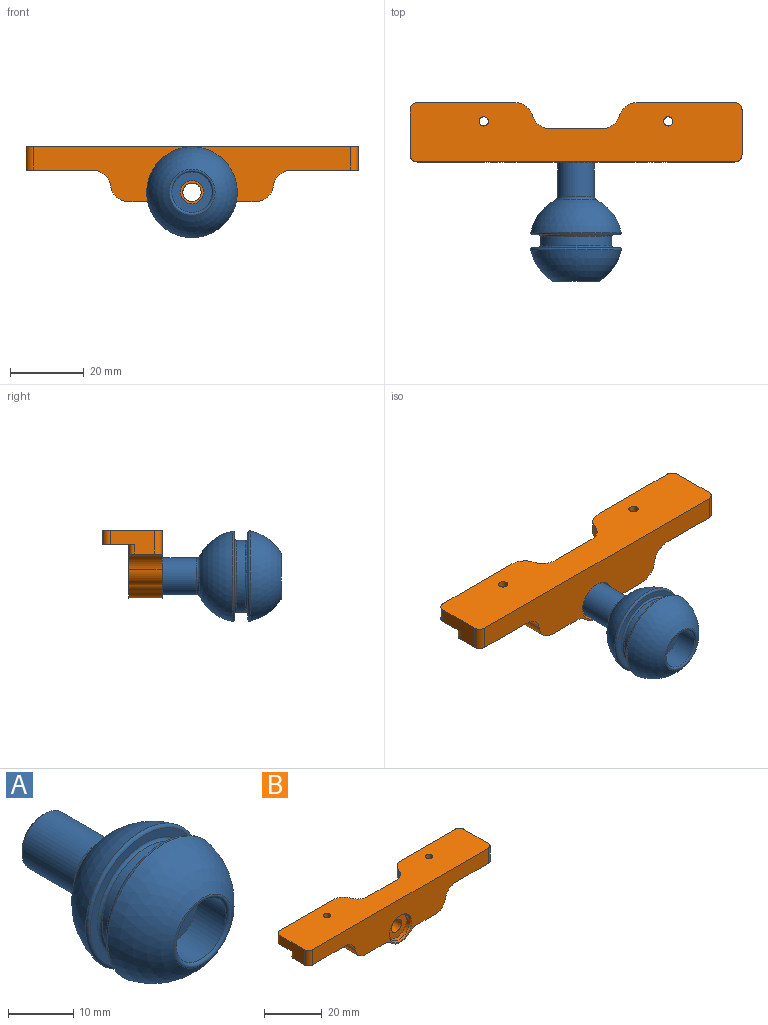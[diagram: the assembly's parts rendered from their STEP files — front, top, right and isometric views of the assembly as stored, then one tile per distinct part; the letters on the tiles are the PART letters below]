
ASSEMBLY  parts=2 mates=1
PART A: 17 faces, bbox 26.6x34.8x26.6 mm
  f0: cylinder r=5mm len=11.36mm, axis (0,-1,0), area 357mm2, adj f15,f16
  f1: sphere r=12.5mm, area 691.3mm2, adj f10,f15
  f2: plane 23.56x23.56mm, normal (0,-1,0), area 105.7mm2, adj f10,f11
  f3: cylinder r=9.75mm len=19.5mm, axis (0,-1,0), area 159.3mm2, adj f11,f12
  f4: plane 23.56x23.56mm, normal (0,1,0), area 105.7mm2, adj f12,f13
  f5: sphere r=12.5mm, area 662.1mm2, adj f13,f14
  f6: cylinder r=5.5mm len=11mm, axis (0,-1,0), area 213.1mm2, adj f7,f14
  f7: plane 11x11mm, normal (0,-1,0), area 63.9mm2, adj f6,f8
  f8: cylinder r=3.15mm len=28.18mm, axis (0,-1,0), area 557.8mm2, adj f7,f9
  f9: plane 9x9mm, normal (0,1,0), area 32.4mm2, adj f8,f16
  f10: torus R=11.78mm, axis (0,-1,0), area 67.1mm2, adj f1,f2
  f11: torus R=10.25mm, axis (0,-1,0), area 49mm2, adj f2,f3
  f12: torus R=10.25mm, axis (0,1,0), area 49mm2, adj f3,f4
  f13: torus R=11.78mm, axis (0,1,0), area 67.1mm2, adj f4,f5
  f14: torus R=6mm, axis (0,1,0), area 38.1mm2, adj f5,f6
  f15: torus R=6mm, axis (0,-1,0), area 36.2mm2, adj f0,f1
  f16: cone r=5mm half-angle=45deg, axis (0,-1,0), area 21.1mm2, adj f0,f9
PART B: 36 faces, bbox 90x16.1x18.4 mm
  f0: cylinder r=2.5mm len=7mm, axis (0,-1,0), area 110mm2, adj f9,f34
  f1: plane 18x9mm, normal (0,0,-1), area 160.7mm2, adj f4,f9,f16,f22,f23,f30
  f2: plane 26.43x3.8mm, normal (0,1,0), area 100.4mm2, adj f5,f11,f14,f25
  f3: plane 12.1x6.4mm, normal (-1,0,0), area 60.3mm2, adj f11,f12,f13,f15,f24,f26
  f4: plane 12.1x6.4mm, normal (1,0,0), area 60.3mm2, adj f1,f11,f14,f16,f23,f25
  f5: cylinder r=5mm len=4.79mm, axis (0,0,-1), area 24.3mm2, adj f2,f6,f11,f14
  f6: cylinder r=5mm len=4.79mm, axis (0,0,-1), area 24.3mm2, adj f5,f9,f11,f14
  f7: cylinder r=5mm len=4.79mm, axis (0,0,-1), area 24.3mm2, adj f8,f9,f11,f13
  f8: cylinder r=5mm len=4.79mm, axis (0,0,-1), area 24.3mm2, adj f7,f10,f11,f13
  f9: plane 87x18.4mm, normal (0,1,0), area 667mm2, adj f0,f1,f6,f7,f11,f12,f13,f14
  f10: plane 26.43x3.8mm, normal (0,1,0), area 100.4mm2, adj f8,f11,f13,f26
  f11: plane 90x16.1mm, normal (0,0,1), area 1268.4mm2, adj f2,f3,f4,f5,f6,f7,f8,f9
  f12: plane 18x9mm, normal (0,0,-1), area 160.7mm2, adj f3,f9,f15,f22,f24,f27
  f13: plane 38x8.6mm, normal (0,0,-1), area 230.5mm2, adj f3,f7,f8,f9,f10,f15,f18,f26
  f14: plane 38x8.6mm, normal (0,0,-1), area 230.5mm2, adj f2,f4,f5,f6,f9,f16,f17,f25
  f15: cylinder r=1.5mm len=2.6mm, axis (0,0,-1), area 6.1mm2, adj f3,f9,f12,f13
  f16: cylinder r=1.5mm len=2.6mm, axis (0,0,1), area 6.1mm2, adj f1,f4,f9,f14
  f17: cylinder r=1.25mm len=3.8mm, axis (0,0,1), area 29.8mm2, adj f11,f14
  f18: cylinder r=1.25mm len=3.8mm, axis (0,0,1), area 29.8mm2, adj f11,f13
  f19: plane 9.15x9mm, normal (0,0,-1), area 82.3mm2, adj f9,f22,f28,f31
  f20: cylinder r=6mm len=9mm, axis (0,1,0), area 87.3mm2, adj f9,f22,f28,f29
  f21: plane 9.15x9mm, normal (0,0,-1), area 82.3mm2, adj f9,f22,f29,f32
  f22: plane 86x18.4mm, normal (0,-1,0), area 862.6mm2, adj f1,f11,f12,f19,f20,f21,f23,f24
  f23: cylinder r=2mm len=6.4mm, axis (0,0,1), area 20.1mm2, adj f1,f4,f11,f22
  f24: cylinder r=2mm len=6.4mm, axis (0,0,-1), area 20.1mm2, adj f3,f11,f12,f22
  f25: cylinder r=2mm len=3.8mm, axis (0,0,-1), area 11.9mm2, adj f2,f4,f11,f14
  f26: cylinder r=2mm len=3.8mm, axis (0,0,-1), area 11.9mm2, adj f3,f10,f11,f13
  f27: cylinder r=5mm len=9mm, axis (0,-1,0), area 64.4mm2, adj f9,f12,f22,f31
  f28: cylinder r=5mm len=9mm, axis (0,1,0), area 36.4mm2, adj f9,f19,f20,f22
  f29: cylinder r=5mm len=9mm, axis (0,1,0), area 36.4mm2, adj f9,f20,f21,f22
  f30: cylinder r=5mm len=9mm, axis (0,1,0), area 64.4mm2, adj f1,f9,f22,f32
  f31: cylinder r=5mm len=9mm, axis (0,-1,0), area 64.4mm2, adj f9,f19,f22,f27
  f32: cylinder r=5mm len=9mm, axis (0,1,0), area 64.4mm2, adj f9,f21,f22,f30
  f33: cylinder r=5mm len=10mm, axis (0,-1,0), area 47.1mm2, adj f34,f35
  f34: plane 10x10mm, normal (0,-1,0), area 58.9mm2, adj f0,f33
  f35: cone r=5mm half-angle=45deg, axis (0,-1,0), area 23.3mm2, adj f22,f33
PLACE A t=(0,-26.78,-6)mm
PLACE B at identity
MATE revolute A.f0 <-> B.f33  axis (0,-1,0) through (0,-9.05,-6)mm
